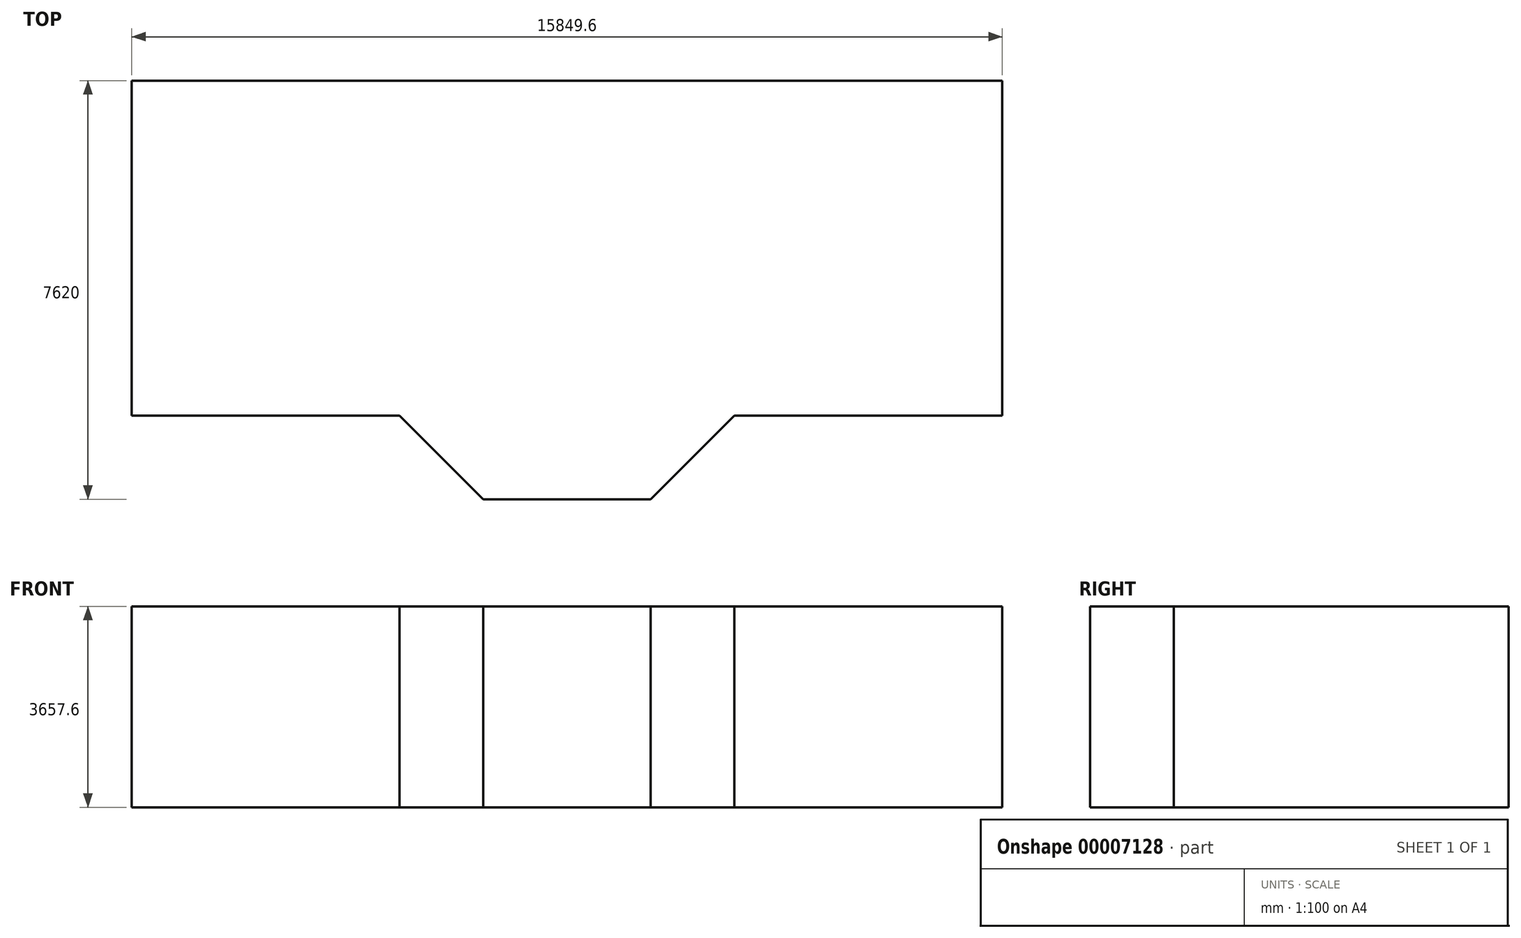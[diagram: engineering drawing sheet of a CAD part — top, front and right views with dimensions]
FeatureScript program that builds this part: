
annotation { "Feature Type Name" : "Feature", "Feature Type Description" : "" }
export const myFeature = defineFeature(function(context is Context, id is Id, definition is map)
    precondition{}
    {
        {
            var Q0;
            Q0=qCreatedBy(makeId("Top.planeOp"),FACE);
            var sketch = newSketch(context, id + "F0", { "sketchPlane" : qUnion([Q0])});
            skLineSegment(sketch, "E0.bottom", {"start": v(822.47, 0) * mm, "end": v(-2225.53, 0) * mm});
            skLineSegment(sketch, "E0.top", {"start": v(822.47, 1524) * mm, "end": v(-2225.53, 1524) * mm});
            skLineSegment(sketch, "E0.left", {"start": v(822.47, 0) * mm, "end": v(822.47, 1524) * mm});
            skLineSegment(sketch, "E0.right", {"start": v(-2225.53, 0) * mm, "end": v(-2225.53, 1524) * mm});
            skLineSegment(sketch, "E1.bottom", {"start": v(822.47, 1524) * mm, "end": v(822.47, 1524) * mm});
            skLineSegment(sketch, "E1.top", {"start": v(822.47, 4572) * mm, "end": v(822.47, 4572) * mm});
            skLineSegment(sketch, "E1.left", {"start": v(822.47, 1524) * mm, "end": v(822.47, 4572) * mm});
            skLineSegment(sketch, "E1.right", {"start": v(822.47, 1524) * mm, "end": v(822.47, 4572) * mm});
            skLineSegment(sketch, "E2.bottom", {"start": v(2346.47, 4572) * mm, "end": v(822.47, 4572) * mm});
            skLineSegment(sketch, "E2.top", {"start": v(2346.47, 1524) * mm, "end": v(822.47, 1524) * mm});
            skLineSegment(sketch, "E2.left", {"start": v(2346.47, 4572) * mm, "end": v(2346.47, 1524) * mm});
            skLineSegment(sketch, "E2.right", {"start": v(822.47, 4572) * mm, "end": v(822.47, 1524) * mm});
            skLineSegment(sketch, "E3.bottom", {"start": v(-2225.53, 1524) * mm, "end": v(-2225.53, 1524) * mm});
            skLineSegment(sketch, "E3.top", {"start": v(-2225.53, 5281.59) * mm, "end": v(-2225.53, 5281.59) * mm});
            skLineSegment(sketch, "E3.left", {"start": v(-2225.53, 1524) * mm, "end": v(-2225.53, 5281.59) * mm});
            skLineSegment(sketch, "E3.right", {"start": v(-2225.53, 1524) * mm, "end": v(-2225.53, 5281.59) * mm});
            skLineSegment(sketch, "E4.bottom", {"start": v(-3749.53, 4572) * mm, "end": v(-2225.53, 4572) * mm});
            skLineSegment(sketch, "E4.top", {"start": v(-3749.53, 1524) * mm, "end": v(-2225.53, 1524) * mm});
            skLineSegment(sketch, "E4.left", {"start": v(-3749.53, 4572) * mm, "end": v(-3749.53, 1524) * mm});
            skLineSegment(sketch, "E4.right", {"start": v(-2225.53, 4572) * mm, "end": v(-2225.53, 1524) * mm});
            skLineSegment(sketch, "E5", {"start": v(822.47, 0) * mm, "end": v(2346.47, 1524) * mm});
            skLineSegment(sketch, "E6", {"start": v(-2225.53, 0) * mm, "end": v(-3749.53, 1524) * mm});
            skLineSegment(sketch, "E7.bottom", {"start": v(-3749.53, 4572) * mm, "end": v(-3749.53, 4572) * mm});
            skLineSegment(sketch, "E7.top", {"start": v(-3749.53, 7620) * mm, "end": v(-3749.53, 7620) * mm});
            skLineSegment(sketch, "E7.left", {"start": v(-3749.53, 4572) * mm, "end": v(-3749.53, 7620) * mm});
            skLineSegment(sketch, "E7.right", {"start": v(-3749.53, 4572) * mm, "end": v(-3749.53, 7620) * mm});
            skLineSegment(sketch, "E8.bottom", {"start": v(2346.47, 4572) * mm, "end": v(-3749.53, 4572) * mm});
            skLineSegment(sketch, "E8.top", {"start": v(2346.47, 7620) * mm, "end": v(-3749.53, 7620) * mm});
            skLineSegment(sketch, "E8.left", {"start": v(2346.47, 4572) * mm, "end": v(2346.47, 7620) * mm});
            skLineSegment(sketch, "E9.bottom", {"start": v(2346.47, 7620) * mm, "end": v(2346.47, 7620) * mm});
            skLineSegment(sketch, "E9.top", {"start": v(2346.47, 1524) * mm, "end": v(2346.47, 1524) * mm});
            skLineSegment(sketch, "E9.left", {"start": v(2346.47, 7620) * mm, "end": v(2346.47, 1524) * mm});
            skLineSegment(sketch, "E9.right", {"start": v(2346.47, 7620) * mm, "end": v(2346.47, 1524) * mm});
            skLineSegment(sketch, "E10.bottom", {"start": v(7223.27, 1524) * mm, "end": v(2346.47, 1524) * mm});
            skLineSegment(sketch, "E10.top", {"start": v(7223.27, 1524) * mm, "end": v(2346.47, 1524) * mm});
            skLineSegment(sketch, "E10.left", {"start": v(7223.27, 1524) * mm, "end": v(7223.27, 1524) * mm});
            skLineSegment(sketch, "E11.bottom", {"start": v(2346.47, 7620) * mm, "end": v(7223.27, 7620) * mm});
            skLineSegment(sketch, "E11.top", {"start": v(2346.47, 1524) * mm, "end": v(7223.27, 1524) * mm});
            skLineSegment(sketch, "E11.right", {"start": v(7223.27, 7620) * mm, "end": v(7223.27, 1524) * mm});
            skLineSegment(sketch, "E12.bottom", {"start": v(-3749.53, 7620) * mm, "end": v(-8626.33, 7620) * mm});
            skLineSegment(sketch, "E12.top", {"start": v(-3749.53, 1524) * mm, "end": v(-8626.33, 1524) * mm});
            skLineSegment(sketch, "E12.left", {"start": v(-3749.53, 7620) * mm, "end": v(-3749.53, 1524) * mm});
            skLineSegment(sketch, "E12.right", {"start": v(-8626.33, 7620) * mm, "end": v(-8626.33, 1524) * mm});
            skSolve(sketch);
        }
        {
            var Q0;
            Q0 = qSketchRegion(id + "F0", true);
            var Q1;
            Q1=makeQuery(id+"F0.imprint","IMPRINT",FACE,{"disambiguationData":[TD([[makeQuery(id+"F0.imprint","IMPRINT",EDGE,{"derivedFrom":sQuery(id+"F0.wireOp",EDGE,"E0.top")}),-1.0]])]});
            var Q2;
            Q2=sQuery(id+"F0.wireOp",EDGE,"E5");
            var Q3;
            Q3=sQuery(id+"F0.wireOp",EDGE,"E0.bottom");
            var Q4;
            Q4=sQuery(id+"F0.wireOp",EDGE,"E6");
            var Q5;
            Q5=sQuery(id+"F0.wireOp",EDGE,"E4.left");
            var Q6;
            Q6=sQuery(id+"F0.wireOp",EDGE,"E2.left");
            var Q7;
            Q7=sQuery(id+"F0.wireOp",EDGE,"E8.left");
            var Q8;
            Q8=sQuery(id+"F0.wireOp",EDGE,"E8.top");
            var Q9;
            Q9=sQuery(id+"F0.wireOp",EDGE,"E7.right");
            extrude(context, id + "F1", {"entities" : qUnion([Q0, Q1]), "surfaceEntities" : qUnion([Q2, Q3, Q4, Q5, Q6, Q7, Q8, Q9]), "endBound" : BoundingType.SYMMETRIC, "depth" : 3657.6 * mm});
        }
    });
